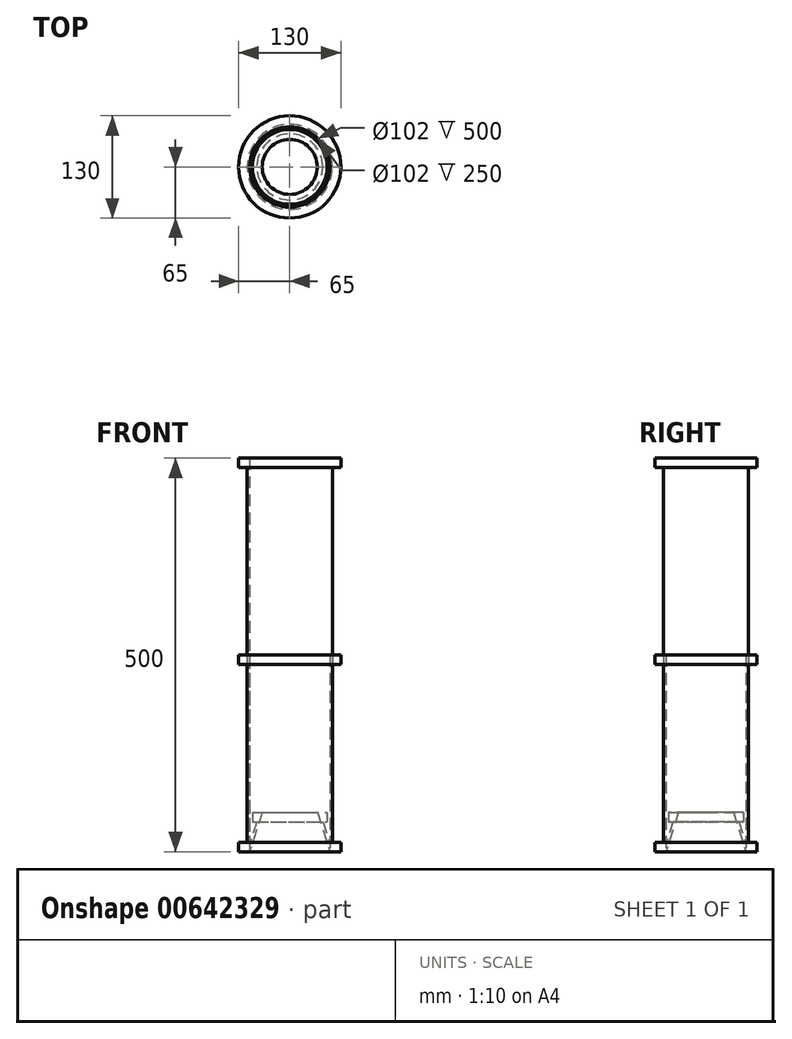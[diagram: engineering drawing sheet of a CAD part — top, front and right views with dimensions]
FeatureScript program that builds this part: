
annotation { "Feature Type Name" : "Feature", "Feature Type Description" : "" }
export const myFeature = defineFeature(function(context is Context, id is Id, definition is map)
    precondition{}
    {
        {
            var Q0;
            Q0=qCreatedBy(makeId("Front.planeOp"),FACE);
            var sketch = newSketch(context, id + "F0", { "sketchPlane" : qUnion([Q0])});
            skLineSegment(sketch, "E0", {"start": v(51, 0) * mm, "end": v(65, 0) * mm});
            skLineSegment(sketch, "E1", {"start": v(65, 0) * mm, "end": v(65, 12) * mm});
            skLineSegment(sketch, "E2", {"start": v(65, 12) * mm, "end": v(54, 12) * mm});
            skLineSegment(sketch, "E3", {"start": v(54, 12) * mm, "end": v(54, 488) * mm});
            skLineSegment(sketch, "E4", {"start": v(54, 488) * mm, "end": v(65, 488) * mm});
            skLineSegment(sketch, "E5", {"start": v(65, 488) * mm, "end": v(65, 500) * mm});
            skLineSegment(sketch, "E6", {"start": v(65, 500) * mm, "end": v(51, 500) * mm});
            skLineSegment(sketch, "E7", {"start": v(51, 500) * mm, "end": v(51, 0) * mm});
            skSolve(sketch);
        }
        {
            var Q0;
            Q0=qCreatedBy(makeId("Front.planeOp"),FACE);
            var sketch = newSketch(context, id + "F1", { "sketchPlane" : qUnion([Q0])});
            skLineSegment(sketch, "E8", {"start": v(0, 0) * mm, "end": v(0, 143.66) * mm, "construction": true});
            skSolve(sketch);
        }
        {
            var Q0;
            Q0 = qSketchRegion(id + "F0", true);
            var Q1;
            Q1=sQuery(id+"F1.wireOp",EDGE,"E8");
            revolve(context, id + "F2", {"entities" : qUnion([Q0]), "axis" : qUnion([Q1]), "revolveType" : RevolveType.FULL});
        }
        {
            var Q0;
            Q0=qCreatedBy(makeId("Front.planeOp"),FACE);
            var sketch = newSketch(context, id + "F3", { "sketchPlane" : qUnion([Q0])});
            skLineSegment(sketch, "E9", {"start": v(51, 0) * mm, "end": v(65, 0) * mm});
            skLineSegment(sketch, "E10", {"start": v(65, 0) * mm, "end": v(65, 12) * mm});
            skLineSegment(sketch, "E11", {"start": v(65, 12) * mm, "end": v(50.3, 12) * mm});
            skLineSegment(sketch, "E12", {"start": v(50.3, 12) * mm, "end": v(41.99, 38) * mm});
            skLineSegment(sketch, "E13", {"start": v(41.99, 38) * mm, "end": v(47.5, 38) * mm});
            skLineSegment(sketch, "E14", {"start": v(47.5, 38) * mm, "end": v(47.5, 50) * mm});
            skLineSegment(sketch, "E15", {"start": v(47.5, 50) * mm, "end": v(35, 50) * mm});
            skLineSegment(sketch, "E16", {"start": v(35, 50) * mm, "end": v(51, 0) * mm});
            skSolve(sketch);
        }
        {
            var Q0;
            Q0 = qSketchRegion(id + "F3", true);
            var Q1;
            Q1=sQuery(id+"F1.wireOp",EDGE,"E8");
            revolve(context, id + "F4", {"entities" : qUnion([Q0]), "axis" : qUnion([Q1]), "revolveType" : RevolveType.FULL});
        }
        {
            var Q0;
            Q0=qCreatedBy(makeId("Front.planeOp"),FACE);
            var sketch = newSketch(context, id + "F5", { "sketchPlane" : qUnion([Q0])});
            skLineSegment(sketch, "E17", {"start": v(51, 0) * mm, "end": v(65, 0) * mm});
            skLineSegment(sketch, "E18", {"start": v(65, 0) * mm, "end": v(65, 12) * mm});
            skLineSegment(sketch, "E19", {"start": v(65, 12) * mm, "end": v(54, 12) * mm});
            skLineSegment(sketch, "E20", {"start": v(54, 12) * mm, "end": v(54, 238) * mm});
            skLineSegment(sketch, "E21", {"start": v(54, 238) * mm, "end": v(65, 238) * mm});
            skLineSegment(sketch, "E22", {"start": v(65, 238) * mm, "end": v(65, 250) * mm});
            skLineSegment(sketch, "E23", {"start": v(65, 250) * mm, "end": v(51, 250) * mm});
            skLineSegment(sketch, "E24", {"start": v(51, 250) * mm, "end": v(51, 0) * mm});
            skSolve(sketch);
        }
        {
            var Q0;
            Q0 = qSketchRegion(id + "F5", true);
            var Q1;
            Q1=sQuery(id+"F1.wireOp",EDGE,"E8");
            revolve(context, id + "F6", {"entities" : qUnion([Q0]), "axis" : qUnion([Q1]), "revolveType" : RevolveType.FULL});
        }
    });
